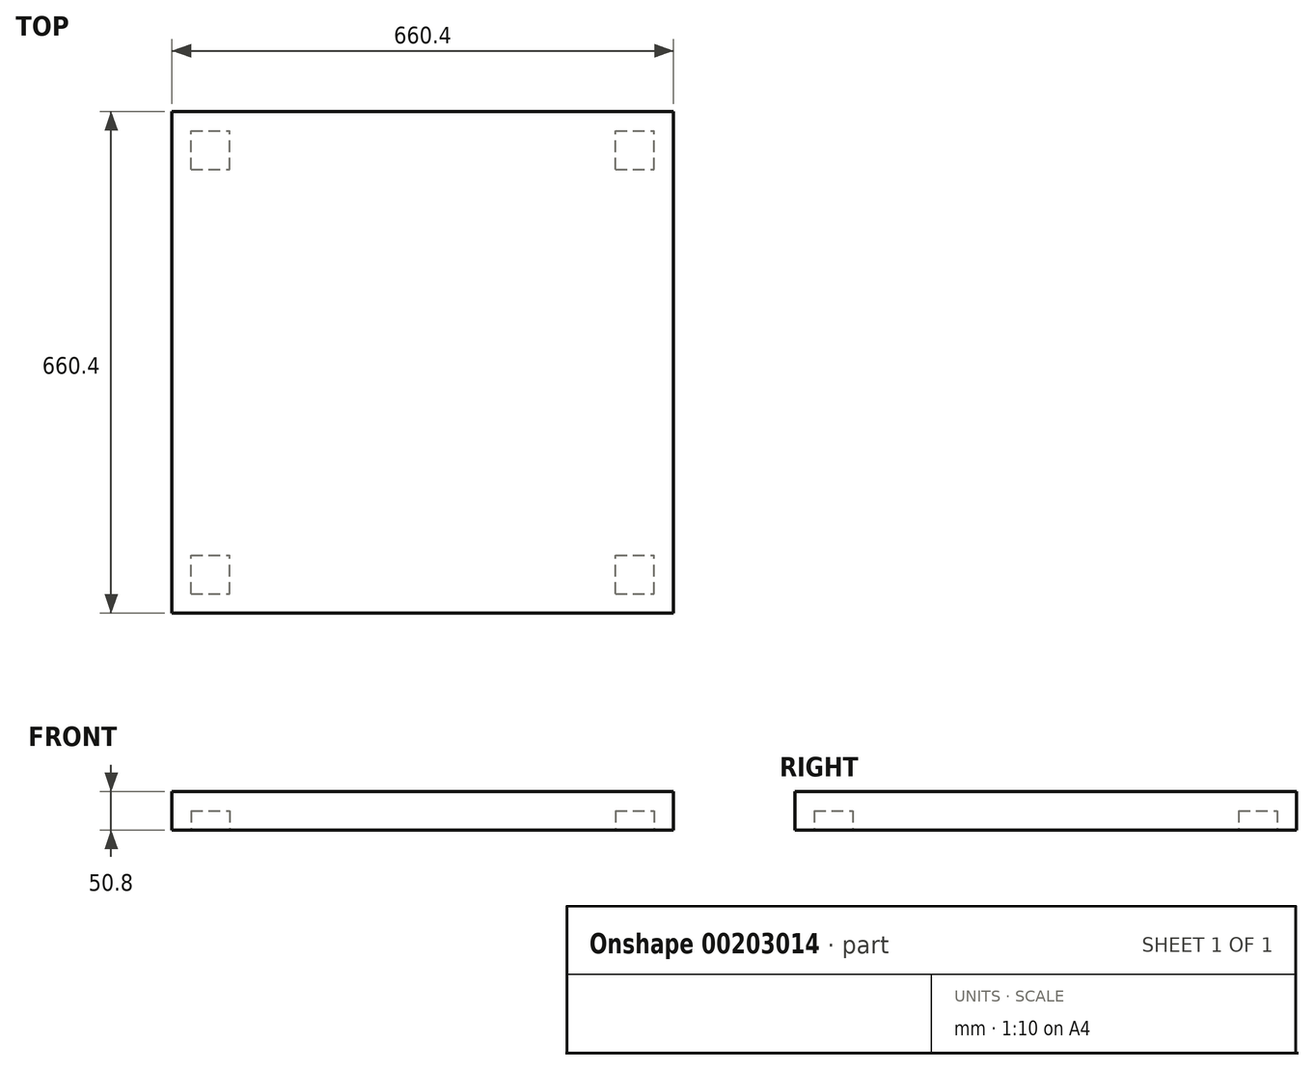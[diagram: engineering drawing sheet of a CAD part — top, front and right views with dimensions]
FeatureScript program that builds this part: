
annotation { "Feature Type Name" : "Feature", "Feature Type Description" : "" }
export const myFeature = defineFeature(function(context is Context, id is Id, definition is map)
    precondition{}
    {
        {
            var Q0;
            Q0=qCreatedBy(makeId("Top.planeOp"),FACE);
            var sketch = newSketch(context, id + "F0", { "sketchPlane" : qUnion([Q0])});
            skLineSegment(sketch, "E0.bottom", {"start": v(-340.26, -164.17) * mm, "end": v(320.14, -164.17) * mm});
            skLineSegment(sketch, "E0.top", {"start": v(-340.26, 496.23) * mm, "end": v(320.14, 496.23) * mm});
            skLineSegment(sketch, "E0.left", {"start": v(-340.26, -164.17) * mm, "end": v(-340.26, 496.23) * mm});
            skLineSegment(sketch, "E0.right", {"start": v(320.14, -164.17) * mm, "end": v(320.14, 496.23) * mm});
            skLineSegment(sketch, "E1.0", {"start": v(-340.26, -138.77) * mm, "end": v(320.14, -138.77) * mm});
            skLineSegment(sketch, "E2.0", {"start": v(-314.86, -164.17) * mm, "end": v(-314.86, 496.23) * mm});
            skLineSegment(sketch, "E3.0", {"start": v(-340.26, 470.83) * mm, "end": v(320.14, 470.83) * mm});
            skLineSegment(sketch, "E4.0", {"start": v(294.74, -164.17) * mm, "end": v(294.74, 496.23) * mm});
            skLineSegment(sketch, "E5.0", {"start": v(-340.26, -87.97) * mm, "end": v(320.14, -87.97) * mm});
            skLineSegment(sketch, "E6.0", {"start": v(-264.06, -164.17) * mm, "end": v(-264.06, 496.23) * mm});
            skLineSegment(sketch, "E7.0", {"start": v(-340.26, 420.03) * mm, "end": v(320.14, 420.03) * mm});
            skLineSegment(sketch, "E8.0", {"start": v(243.94, -164.17) * mm, "end": v(243.94, 496.23) * mm});
            skSolve(sketch);
        }
        {
            var Q0;
            {var subQ0=sQuery(id+"F0.wireOp",EDGE,"E1.0");var subQ1=sQuery(id+"F0.wireOp",EDGE,"E0.right");var subQ2=makeQuery(id+"F0.imprint","INTERSECT",VERTEX,{"derivedFrom":[subQ1,subQ0]});Q0=makeQuery(id+"F0.imprint","IMPRINT",FACE,{"disambiguationData":[TD([[makeQuery(id+"F0.imprint","IMPRINT",EDGE,{"disambiguationData":[TD([[subQ2,-1.0]])],"derivedFrom":subQ1}),1.0]])]});}
            var Q1;
            {var subQ0=sQuery(id+"F0.wireOp",EDGE,"E2.0");var subQ1=sQuery(id+"F0.wireOp",EDGE,"E0.bottom");var subQ2=makeQuery(id+"F0.imprint","INTERSECT",VERTEX,{"derivedFrom":[subQ1,subQ0]});Q1=makeQuery(id+"F0.imprint","IMPRINT",FACE,{"disambiguationData":[TD([[makeQuery(id+"F0.imprint","IMPRINT",EDGE,{"disambiguationData":[TD([[subQ2,-1.0]])],"derivedFrom":subQ1}),1.0]])]});}
            var Q2;
            {var subQ0=sQuery(id+"F0.wireOp",EDGE,"E0.right");var subQ1=sQuery(id+"F0.wireOp",EDGE,"E0.top");var subQ2=makeQuery(id+"F0.imprint","INTERSECT",VERTEX,{"derivedFrom":[subQ1,subQ0]});Q2=makeQuery(id+"F0.imprint","IMPRINT",FACE,{"disambiguationData":[TD([[makeQuery(id+"F0.imprint","IMPRINT",EDGE,{"disambiguationData":[TD([[subQ2,1.0]])],"derivedFrom":subQ1}),-1.0]])]});}
            var Q3;
            {var subQ0=sQuery(id+"F0.wireOp",EDGE,"E2.0");var subQ1=sQuery(id+"F0.wireOp",EDGE,"E1.0");var subQ2=makeQuery(id+"F0.imprint","INTERSECT",VERTEX,{"derivedFrom":[subQ1,subQ0]});Q3=makeQuery(id+"F0.imprint","IMPRINT",FACE,{"disambiguationData":[TD([[makeQuery(id+"F0.imprint","IMPRINT",EDGE,{"disambiguationData":[TD([[subQ2,-1.0]])],"derivedFrom":subQ1}),1.0]])]});}
            var Q4;
            {var subQ0=sQuery(id+"F0.wireOp",EDGE,"E0.right");var subQ1=sQuery(id+"F0.wireOp",EDGE,"E0.bottom");var subQ2=makeQuery(id+"F0.imprint","INTERSECT",VERTEX,{"derivedFrom":[subQ1,subQ0]});Q4=makeQuery(id+"F0.imprint","IMPRINT",FACE,{"disambiguationData":[TD([[makeQuery(id+"F0.imprint","IMPRINT",EDGE,{"disambiguationData":[TD([[subQ2,1.0]])],"derivedFrom":subQ1}),1.0]])]});}
            var Q5;
            {var subQ0=sQuery(id+"F0.wireOp",EDGE,"E0.left");var subQ1=sQuery(id+"F0.wireOp",EDGE,"E0.bottom");var subQ2=makeQuery(id+"F0.imprint","INTERSECT",VERTEX,{"derivedFrom":[subQ1,subQ0]});Q5=makeQuery(id+"F0.imprint","IMPRINT",FACE,{"disambiguationData":[TD([[makeQuery(id+"F0.imprint","IMPRINT",EDGE,{"disambiguationData":[TD([[subQ2,-1.0]])],"derivedFrom":subQ1}),1.0]])]});}
            var Q6;
            {var subQ0=sQuery(id+"F0.wireOp",EDGE,"E8.0");var subQ1=sQuery(id+"F0.wireOp",EDGE,"E1.0");var subQ2=makeQuery(id+"F0.imprint","INTERSECT",VERTEX,{"derivedFrom":[subQ1,subQ0]});Q6=makeQuery(id+"F0.imprint","IMPRINT",FACE,{"disambiguationData":[TD([[makeQuery(id+"F0.imprint","IMPRINT",EDGE,{"disambiguationData":[TD([[subQ2,-1.0]])],"derivedFrom":subQ1}),1.0]])]});}
            var Q7;
            {var subQ0=sQuery(id+"F0.wireOp",EDGE,"E6.0");var subQ1=sQuery(id+"F0.wireOp",EDGE,"E0.bottom");var subQ2=makeQuery(id+"F0.imprint","INTERSECT",VERTEX,{"derivedFrom":[subQ1,subQ0]});Q7=makeQuery(id+"F0.imprint","IMPRINT",FACE,{"disambiguationData":[TD([[makeQuery(id+"F0.imprint","IMPRINT",EDGE,{"disambiguationData":[TD([[subQ2,-1.0]])],"derivedFrom":subQ1}),1.0]])]});}
            var Q8;
            {var subQ0=sQuery(id+"F0.wireOp",EDGE,"E4.0");var subQ1=sQuery(id+"F0.wireOp",EDGE,"E0.bottom");var subQ2=makeQuery(id+"F0.imprint","INTERSECT",VERTEX,{"derivedFrom":[subQ1,subQ0]});Q8=makeQuery(id+"F0.imprint","IMPRINT",FACE,{"disambiguationData":[TD([[makeQuery(id+"F0.imprint","IMPRINT",EDGE,{"disambiguationData":[TD([[subQ2,1.0]])],"derivedFrom":subQ1}),1.0]])]});}
            var Q9;
            {var subQ0=sQuery(id+"F0.wireOp",EDGE,"E6.0");var subQ1=sQuery(id+"F0.wireOp",EDGE,"E0.top");var subQ2=makeQuery(id+"F0.imprint","INTERSECT",VERTEX,{"derivedFrom":[subQ1,subQ0]});Q9=makeQuery(id+"F0.imprint","IMPRINT",FACE,{"disambiguationData":[TD([[makeQuery(id+"F0.imprint","IMPRINT",EDGE,{"disambiguationData":[TD([[subQ2,-1.0]])],"derivedFrom":subQ1}),-1.0]])]});}
            var Q10;
            {var subQ0=sQuery(id+"F0.wireOp",EDGE,"E4.0");var subQ1=sQuery(id+"F0.wireOp",EDGE,"E0.top");var subQ2=makeQuery(id+"F0.imprint","INTERSECT",VERTEX,{"derivedFrom":[subQ1,subQ0]});Q10=makeQuery(id+"F0.imprint","IMPRINT",FACE,{"disambiguationData":[TD([[makeQuery(id+"F0.imprint","IMPRINT",EDGE,{"disambiguationData":[TD([[subQ2,1.0]])],"derivedFrom":subQ1}),-1.0]])]});}
            var Q11;
            {var subQ0=sQuery(id+"F0.wireOp",EDGE,"E1.0");var subQ1=sQuery(id+"F0.wireOp",EDGE,"E0.left");var subQ2=makeQuery(id+"F0.imprint","INTERSECT",VERTEX,{"derivedFrom":[subQ1,subQ0]});Q11=makeQuery(id+"F0.imprint","IMPRINT",FACE,{"disambiguationData":[TD([[makeQuery(id+"F0.imprint","IMPRINT",EDGE,{"disambiguationData":[TD([[subQ2,-1.0]])],"derivedFrom":subQ1}),-1.0]])]});}
            var Q12;
            {var subQ0=sQuery(id+"F0.wireOp",EDGE,"E5.0");var subQ1=sQuery(id+"F0.wireOp",EDGE,"E0.left");var subQ2=makeQuery(id+"F0.imprint","INTERSECT",VERTEX,{"derivedFrom":[subQ1,subQ0]});Q12=makeQuery(id+"F0.imprint","IMPRINT",FACE,{"disambiguationData":[TD([[makeQuery(id+"F0.imprint","IMPRINT",EDGE,{"disambiguationData":[TD([[subQ2,-1.0]])],"derivedFrom":subQ1}),-1.0]])]});}
            var Q13;
            {var subQ0=sQuery(id+"F0.wireOp",EDGE,"E5.0");var subQ1=sQuery(id+"F0.wireOp",EDGE,"E4.0");var subQ2=makeQuery(id+"F0.imprint","INTERSECT",VERTEX,{"derivedFrom":[subQ1,subQ0]});Q13=makeQuery(id+"F0.imprint","IMPRINT",FACE,{"disambiguationData":[TD([[makeQuery(id+"F0.imprint","IMPRINT",EDGE,{"disambiguationData":[TD([[subQ2,-1.0]])],"derivedFrom":subQ1}),1.0]])]});}
            var Q14;
            {var subQ0=sQuery(id+"F0.wireOp",EDGE,"E5.0");var subQ1=sQuery(id+"F0.wireOp",EDGE,"E0.right");var subQ2=makeQuery(id+"F0.imprint","INTERSECT",VERTEX,{"derivedFrom":[subQ1,subQ0]});Q14=makeQuery(id+"F0.imprint","IMPRINT",FACE,{"disambiguationData":[TD([[makeQuery(id+"F0.imprint","IMPRINT",EDGE,{"disambiguationData":[TD([[subQ2,-1.0]])],"derivedFrom":subQ1}),1.0]])]});}
            var Q15;
            {var subQ0=sQuery(id+"F0.wireOp",EDGE,"E3.0");var subQ1=sQuery(id+"F0.wireOp",EDGE,"E0.right");var subQ2=makeQuery(id+"F0.imprint","INTERSECT",VERTEX,{"derivedFrom":[subQ1,subQ0]});Q15=makeQuery(id+"F0.imprint","IMPRINT",FACE,{"disambiguationData":[TD([[makeQuery(id+"F0.imprint","IMPRINT",EDGE,{"disambiguationData":[TD([[subQ2,1.0]])],"derivedFrom":subQ1}),1.0]])]});}
            var Q16;
            {var subQ0=sQuery(id+"F0.wireOp",EDGE,"E8.0");var subQ1=sQuery(id+"F0.wireOp",EDGE,"E3.0");var subQ2=makeQuery(id+"F0.imprint","INTERSECT",VERTEX,{"derivedFrom":[subQ1,subQ0]});Q16=makeQuery(id+"F0.imprint","IMPRINT",FACE,{"disambiguationData":[TD([[makeQuery(id+"F0.imprint","IMPRINT",EDGE,{"disambiguationData":[TD([[subQ2,-1.0]])],"derivedFrom":subQ1}),-1.0]])]});}
            var Q17;
            {var subQ0=sQuery(id+"F0.wireOp",EDGE,"E6.0");var subQ1=sQuery(id+"F0.wireOp",EDGE,"E5.0");var subQ2=makeQuery(id+"F0.imprint","INTERSECT",VERTEX,{"derivedFrom":[subQ1,subQ0]});Q17=makeQuery(id+"F0.imprint","IMPRINT",FACE,{"disambiguationData":[TD([[makeQuery(id+"F0.imprint","IMPRINT",EDGE,{"disambiguationData":[TD([[subQ2,-1.0]])],"derivedFrom":subQ1}),1.0]])]});}
            var Q18;
            {var subQ0=sQuery(id+"F0.wireOp",EDGE,"E6.0");var subQ1=sQuery(id+"F0.wireOp",EDGE,"E1.0");var subQ2=makeQuery(id+"F0.imprint","INTERSECT",VERTEX,{"derivedFrom":[subQ1,subQ0]});Q18=makeQuery(id+"F0.imprint","IMPRINT",FACE,{"disambiguationData":[TD([[makeQuery(id+"F0.imprint","IMPRINT",EDGE,{"disambiguationData":[TD([[subQ2,-1.0]])],"derivedFrom":subQ1}),1.0]])]});}
            var Q19;
            {var subQ0=sQuery(id+"F0.wireOp",EDGE,"E5.0");var subQ1=sQuery(id+"F0.wireOp",EDGE,"E2.0");var subQ2=makeQuery(id+"F0.imprint","INTERSECT",VERTEX,{"derivedFrom":[subQ1,subQ0]});Q19=makeQuery(id+"F0.imprint","IMPRINT",FACE,{"disambiguationData":[TD([[makeQuery(id+"F0.imprint","IMPRINT",EDGE,{"disambiguationData":[TD([[subQ2,-1.0]])],"derivedFrom":subQ1}),-1.0]])]});}
            var Q20;
            {var subQ0=sQuery(id+"F0.wireOp",EDGE,"E6.0");var subQ1=sQuery(id+"F0.wireOp",EDGE,"E3.0");var subQ2=makeQuery(id+"F0.imprint","INTERSECT",VERTEX,{"derivedFrom":[subQ1,subQ0]});Q20=makeQuery(id+"F0.imprint","IMPRINT",FACE,{"disambiguationData":[TD([[makeQuery(id+"F0.imprint","IMPRINT",EDGE,{"disambiguationData":[TD([[subQ2,-1.0]])],"derivedFrom":subQ1}),-1.0]])]});}
            var Q21;
            {var subQ0=sQuery(id+"F0.wireOp",EDGE,"E7.0");var subQ1=sQuery(id+"F0.wireOp",EDGE,"E2.0");var subQ2=makeQuery(id+"F0.imprint","INTERSECT",VERTEX,{"derivedFrom":[subQ1,subQ0]});Q21=makeQuery(id+"F0.imprint","IMPRINT",FACE,{"disambiguationData":[TD([[makeQuery(id+"F0.imprint","IMPRINT",EDGE,{"disambiguationData":[TD([[subQ2,-1.0]])],"derivedFrom":subQ1}),-1.0]])]});}
            var Q22;
            {var subQ0=sQuery(id+"F0.wireOp",EDGE,"E3.0");var subQ1=sQuery(id+"F0.wireOp",EDGE,"E0.left");var subQ2=makeQuery(id+"F0.imprint","INTERSECT",VERTEX,{"derivedFrom":[subQ1,subQ0]});Q22=makeQuery(id+"F0.imprint","IMPRINT",FACE,{"disambiguationData":[TD([[makeQuery(id+"F0.imprint","IMPRINT",EDGE,{"disambiguationData":[TD([[subQ2,1.0]])],"derivedFrom":subQ1}),-1.0]])]});}
            var Q23;
            {var subQ0=sQuery(id+"F0.wireOp",EDGE,"E0.left");var subQ1=sQuery(id+"F0.wireOp",EDGE,"E0.top");var subQ2=makeQuery(id+"F0.imprint","INTERSECT",VERTEX,{"derivedFrom":[subQ1,subQ0]});Q23=makeQuery(id+"F0.imprint","IMPRINT",FACE,{"disambiguationData":[TD([[makeQuery(id+"F0.imprint","IMPRINT",EDGE,{"disambiguationData":[TD([[subQ2,-1.0]])],"derivedFrom":subQ1}),-1.0]])]});}
            var Q24;
            {var subQ0=sQuery(id+"F0.wireOp",EDGE,"E2.0");var subQ1=sQuery(id+"F0.wireOp",EDGE,"E0.top");var subQ2=makeQuery(id+"F0.imprint","INTERSECT",VERTEX,{"derivedFrom":[subQ1,subQ0]});Q24=makeQuery(id+"F0.imprint","IMPRINT",FACE,{"disambiguationData":[TD([[makeQuery(id+"F0.imprint","IMPRINT",EDGE,{"disambiguationData":[TD([[subQ2,-1.0]])],"derivedFrom":subQ1}),-1.0]])]});}
            var Q25;
            Q25=sQuery(id+"F0.wireOp",EDGE,"E8.0");
            var Q26;
            Q26=sQuery(id+"F0.wireOp",EDGE,"E7.0");
            var Q27;
            Q27=sQuery(id+"F0.wireOp",EDGE,"E5.0");
            var Q28;
            Q28=sQuery(id+"F0.wireOp",EDGE,"E6.0");
            var Q29;
            Q29=sQuery(id+"F0.wireOp",EDGE,"E4.0");
            var Q30;
            Q30=sQuery(id+"F0.wireOp",EDGE,"E3.0");
            var Q31;
            Q31=sQuery(id+"F0.wireOp",EDGE,"E1.0");
            var Q32;
            Q32=sQuery(id+"F0.wireOp",EDGE,"E0.right");
            var Q33;
            Q33=sQuery(id+"F0.wireOp",EDGE,"E2.0");
            var Q34;
            Q34=sQuery(id+"F0.wireOp",EDGE,"E0.left");
            var Q35;
            Q35=sQuery(id+"F0.wireOp",EDGE,"E0.top");
            var Q36;
            Q36=sQuery(id+"F0.wireOp",EDGE,"E0.bottom");
            extrude(context, id + "F1", {"entities" : qUnion([Q0, Q1, Q2, Q3, Q4, Q5, Q6, Q7, Q8, Q9, Q10, Q11, Q12, Q13, Q14, Q15, Q16, Q17, Q18, Q19, Q20, Q21, Q22, Q23, Q24]), "surfaceEntities" : qUnion([Q25, Q26, Q27, Q28, Q29, Q30, Q31, Q32, Q33, Q34, Q35, Q36]), "depth" : 50.8 * mm});
        }
        {
            var Q0;
            {var subQ0=sQuery(id+"F0.wireOp",EDGE,"E8.0");var subQ1=sQuery(id+"F0.wireOp",EDGE,"E1.0");var subQ2=makeQuery(id+"F0.imprint","INTERSECT",VERTEX,{"derivedFrom":[subQ1,subQ0]});Q0=makeQuery(id+"F0.imprint","IMPRINT",FACE,{"disambiguationData":[TD([[makeQuery(id+"F0.imprint","IMPRINT",EDGE,{"disambiguationData":[TD([[subQ2,-1.0]])],"derivedFrom":subQ1}),1.0]])]});}
            extrude(context, id + "F2", {"entities" : qUnion([Q0]), "operationType" : NewBodyOperationType.REMOVE, "depth" : 25.4 * mm});
        }
        {
            var Q0;
            {var subQ0=sQuery(id+"F0.wireOp",EDGE,"E8.0");var subQ1=sQuery(id+"F0.wireOp",EDGE,"E3.0");var subQ2=makeQuery(id+"F0.imprint","INTERSECT",VERTEX,{"derivedFrom":[subQ1,subQ0]});Q0=makeQuery(id+"F0.imprint","IMPRINT",FACE,{"disambiguationData":[TD([[makeQuery(id+"F0.imprint","IMPRINT",EDGE,{"disambiguationData":[TD([[subQ2,-1.0]])],"derivedFrom":subQ1}),-1.0]])]});}
            extrude(context, id + "F3", {"entities" : qUnion([Q0]), "operationType" : NewBodyOperationType.REMOVE, "depth" : 25.4 * mm});
        }
        {
            var Q0;
            {var subQ0=sQuery(id+"F0.wireOp",EDGE,"E7.0");var subQ1=sQuery(id+"F0.wireOp",EDGE,"E2.0");var subQ2=makeQuery(id+"F0.imprint","INTERSECT",VERTEX,{"derivedFrom":[subQ1,subQ0]});Q0=makeQuery(id+"F0.imprint","IMPRINT",FACE,{"disambiguationData":[TD([[makeQuery(id+"F0.imprint","IMPRINT",EDGE,{"disambiguationData":[TD([[subQ2,-1.0]])],"derivedFrom":subQ1}),-1.0]])]});}
            extrude(context, id + "F4", {"entities" : qUnion([Q0]), "operationType" : NewBodyOperationType.REMOVE, "depth" : 25.4 * mm});
        }
        {
            var Q0;
            {var subQ0=sQuery(id+"F0.wireOp",EDGE,"E2.0");var subQ1=sQuery(id+"F0.wireOp",EDGE,"E1.0");var subQ2=makeQuery(id+"F0.imprint","INTERSECT",VERTEX,{"derivedFrom":[subQ1,subQ0]});Q0=makeQuery(id+"F0.imprint","IMPRINT",FACE,{"disambiguationData":[TD([[makeQuery(id+"F0.imprint","IMPRINT",EDGE,{"disambiguationData":[TD([[subQ2,-1.0]])],"derivedFrom":subQ1}),1.0]])]});}
            extrude(context, id + "F5", {"entities" : qUnion([Q0]), "operationType" : NewBodyOperationType.REMOVE, "depth" : 25.4 * mm});
        }
    });
